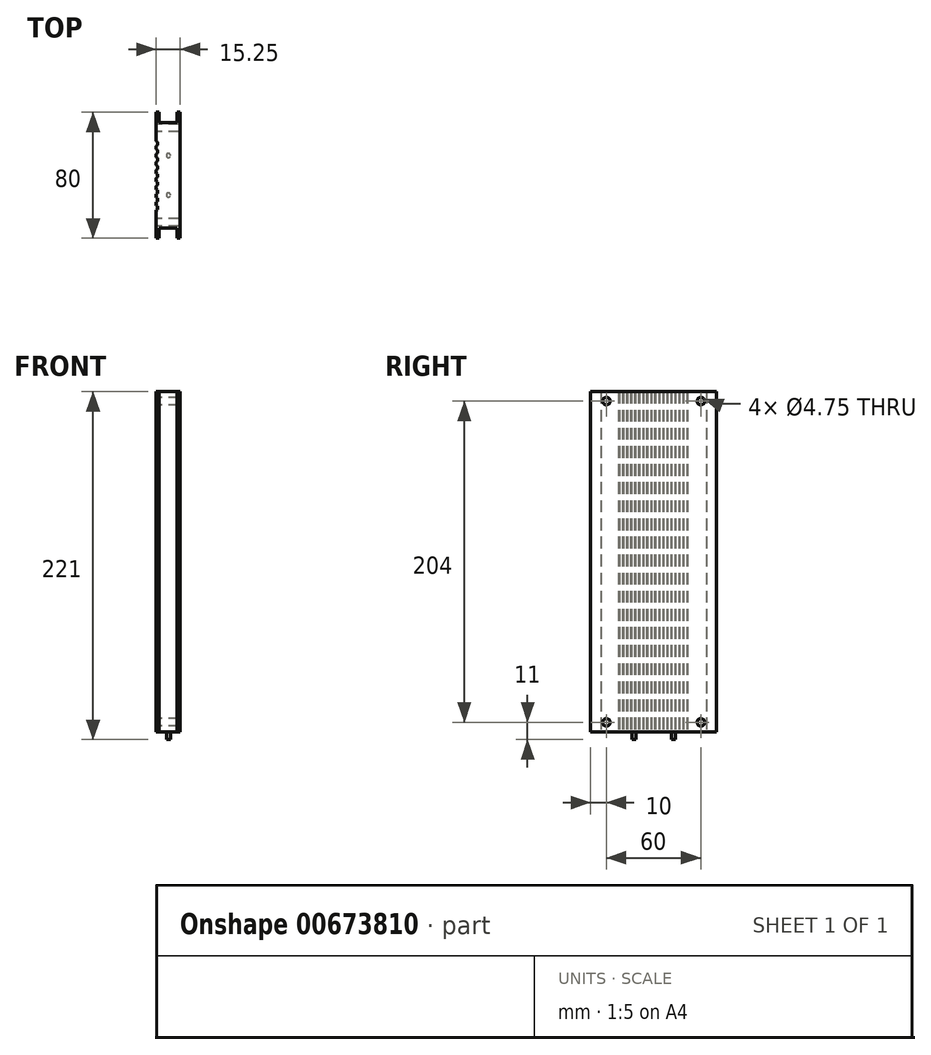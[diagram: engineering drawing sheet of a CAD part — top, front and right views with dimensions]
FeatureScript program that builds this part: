
annotation { "Feature Type Name" : "Feature", "Feature Type Description" : "" }
export const myFeature = defineFeature(function(context is Context, id is Id, definition is map)
    precondition{}
    {
        {
            var Q0;
            Q0=qCreatedBy(makeId("Top.planeOp"),FACE);
            var sketch = newSketch(context, id + "F0", { "sketchPlane" : qUnion([Q0])});
            skLineSegment(sketch, "E0", {"start": v(0, 0) * mm, "end": v(0, 80) * mm});
            skLineSegment(sketch, "E1", {"start": v(0, 80) * mm, "end": v(1.9, 80) * mm});
            skLineSegment(sketch, "E2", {"start": v(1.9, 80) * mm, "end": v(1.9, 73.55) * mm});
            skLineSegment(sketch, "E3", {"start": v(1.9, 73.55) * mm, "end": v(13.35, 73.55) * mm});
            skLineSegment(sketch, "E4", {"start": v(13.35, 73.55) * mm, "end": v(13.35, 80) * mm});
            skLineSegment(sketch, "E5", {"start": v(13.35, 80) * mm, "end": v(15.25, 80) * mm});
            skLineSegment(sketch, "E6", {"start": v(15.25, 80) * mm, "end": v(15.25, 0) * mm});
            skLineSegment(sketch, "E7", {"start": v(15.25, 0) * mm, "end": v(13.35, 0) * mm});
            skLineSegment(sketch, "E8", {"start": v(13.35, 0) * mm, "end": v(13.35, 6.45) * mm});
            skLineSegment(sketch, "E9", {"start": v(13.35, 6.45) * mm, "end": v(1.9, 6.45) * mm});
            skLineSegment(sketch, "E10", {"start": v(1.9, 6.45) * mm, "end": v(1.9, 0) * mm});
            skLineSegment(sketch, "E11", {"start": v(1.9, 0) * mm, "end": v(0, 0) * mm});
            skPoint(sketch, "E12", {"position": v(0, 61.6) * mm});
            skLineSegment(sketch, "E13", {"start": v(0, 61.6) * mm, "end": v(1, 61.1) * mm});
            skLineSegment(sketch, "E14", {"start": v(1, 61.1) * mm, "end": v(1, 59.1) * mm});
            skLineSegment(sketch, "E15", {"start": v(1, 59.1) * mm, "end": v(0, 58.6) * mm});
            skLineSegment(sketch, "E16", {"start": v(0, 58.6) * mm, "end": v(0, 61.6) * mm});
            skLineSegment(sketch, "E17.0.1.0", {"start": v(0, 56.5) * mm, "end": v(1, 56) * mm});
            skPoint(sketch, "E17.0.1.1", {"position": v(0, 56.5) * mm});
            skLineSegment(sketch, "E17.0.1.2", {"start": v(0, 53.5) * mm, "end": v(0, 56.5) * mm});
            skLineSegment(sketch, "E17.0.1.3", {"start": v(1, 54) * mm, "end": v(0, 53.5) * mm});
            skLineSegment(sketch, "E17.0.1.4", {"start": v(1, 56) * mm, "end": v(1, 54) * mm});
            skLineSegment(sketch, "E17.0.2.0", {"start": v(0, 51.4) * mm, "end": v(1, 50.9) * mm});
            skPoint(sketch, "E17.0.2.1", {"position": v(0, 51.4) * mm});
            skLineSegment(sketch, "E17.0.2.2", {"start": v(0, 48.4) * mm, "end": v(0, 51.4) * mm});
            skLineSegment(sketch, "E17.0.2.3", {"start": v(1, 48.9) * mm, "end": v(0, 48.4) * mm});
            skLineSegment(sketch, "E17.0.2.4", {"start": v(1, 50.9) * mm, "end": v(1, 48.9) * mm});
            skLineSegment(sketch, "E17.0.3.0", {"start": v(0, 46.3) * mm, "end": v(1, 45.8) * mm});
            skPoint(sketch, "E17.0.3.1", {"position": v(0, 46.3) * mm});
            skLineSegment(sketch, "E17.0.3.2", {"start": v(0, 43.3) * mm, "end": v(0, 46.3) * mm});
            skLineSegment(sketch, "E17.0.3.3", {"start": v(1, 43.8) * mm, "end": v(0, 43.3) * mm});
            skLineSegment(sketch, "E17.0.3.4", {"start": v(1, 45.8) * mm, "end": v(1, 43.8) * mm});
            skLineSegment(sketch, "E17.0.4.0", {"start": v(0, 41.2) * mm, "end": v(1, 40.7) * mm});
            skPoint(sketch, "E17.0.4.1", {"position": v(0, 41.2) * mm});
            skLineSegment(sketch, "E17.0.4.2", {"start": v(0, 38.2) * mm, "end": v(0, 41.2) * mm});
            skLineSegment(sketch, "E17.0.4.3", {"start": v(1, 38.7) * mm, "end": v(0, 38.2) * mm});
            skLineSegment(sketch, "E17.0.4.4", {"start": v(1, 40.7) * mm, "end": v(1, 38.7) * mm});
            skLineSegment(sketch, "E17.0.5.0", {"start": v(0, 36.1) * mm, "end": v(1, 35.6) * mm});
            skPoint(sketch, "E17.0.5.1", {"position": v(0, 36.1) * mm});
            skLineSegment(sketch, "E17.0.5.2", {"start": v(0, 33.1) * mm, "end": v(0, 36.1) * mm});
            skLineSegment(sketch, "E17.0.5.3", {"start": v(1, 33.6) * mm, "end": v(0, 33.1) * mm});
            skLineSegment(sketch, "E17.0.5.4", {"start": v(1, 35.6) * mm, "end": v(1, 33.6) * mm});
            skLineSegment(sketch, "E17.0.6.0", {"start": v(0, 31) * mm, "end": v(1, 30.5) * mm});
            skPoint(sketch, "E17.0.6.1", {"position": v(0, 31) * mm});
            skLineSegment(sketch, "E17.0.6.2", {"start": v(0, 28) * mm, "end": v(0, 31) * mm});
            skLineSegment(sketch, "E17.0.6.3", {"start": v(1, 28.5) * mm, "end": v(0, 28) * mm});
            skLineSegment(sketch, "E17.0.6.4", {"start": v(1, 30.5) * mm, "end": v(1, 28.5) * mm});
            skLineSegment(sketch, "E17.0.7.0", {"start": v(0, 25.9) * mm, "end": v(1, 25.4) * mm});
            skPoint(sketch, "E17.0.7.1", {"position": v(0, 25.9) * mm});
            skLineSegment(sketch, "E17.0.7.2", {"start": v(0, 22.9) * mm, "end": v(0, 25.9) * mm});
            skLineSegment(sketch, "E17.0.7.3", {"start": v(1, 23.4) * mm, "end": v(0, 22.9) * mm});
            skLineSegment(sketch, "E17.0.7.4", {"start": v(1, 25.4) * mm, "end": v(1, 23.4) * mm});
            skLineSegment(sketch, "E17.0.8.0", {"start": v(0, 20.8) * mm, "end": v(1, 20.3) * mm});
            skPoint(sketch, "E17.0.8.1", {"position": v(0, 20.8) * mm});
            skLineSegment(sketch, "E17.0.8.2", {"start": v(0, 17.8) * mm, "end": v(0, 20.8) * mm});
            skLineSegment(sketch, "E17.0.8.3", {"start": v(1, 18.3) * mm, "end": v(0, 17.8) * mm});
            skLineSegment(sketch, "E17.0.8.4", {"start": v(1, 20.3) * mm, "end": v(1, 18.3) * mm});
            skLineSegment(sketch, "E17.direction1", {"start": v(0, 58.6) * mm, "end": v(25, 58.6) * mm, "construction": true});
            skLineSegment(sketch, "E17.direction2", {"start": v(0, 58.6) * mm, "end": v(0, 53.5) * mm, "construction": true});
            skSolve(sketch);
        }
        {
            var Q0;
            {var subQ3=sQuery(id+"F0.wireOp",EDGE,"E1");Q0=makeQuery(id+"F0.imprint","IMPRINT",FACE,{"disambiguationData":[TD([[makeQuery(id+"F0.imprint","IMPRINT",EDGE,{"derivedFrom":subQ3}),-1.0]])]});}
            extrude(context, id + "F1", {"entities" : qUnion([Q0]), "depth" : 216 * mm, "offsetDistance" : 25 * mm});
        }
        {
            var Q0;
            {var subQ0=sQuery(id+"F0.wireOp",EDGE,"E0");Q0=makeQuery(id+"F1.opExtrude","SWEPT_FACE",FACE,{"disambiguationData":[OSD([subQ0]),TDD([makeQuery(id+"F0.imprint","IMPRINT",EDGE,{"disambiguationData":[TD([[makeQuery(id+"F0.imprint","INTERSECT",VERTEX,{"derivedFrom":[subQ0,sQuery(id+"F0.wireOp",EDGE,"E1")]}),1.0]])],"derivedFrom":subQ0})])]});}
            var sketch = newSketch(context, id + "F2", { "sketchPlane" : qUnion([Q0])});
            skCircle(sketch, "E18", {"center": v(-70, 6) * mm, "radius": 2.38 * mm});
            skCircle(sketch, "E19", {"center": v(-10, 6) * mm, "radius": 2.38 * mm});
            skCircle(sketch, "E20", {"center": v(-70, 210) * mm, "radius": 2.38 * mm});
            skCircle(sketch, "E21", {"center": v(-10, 210) * mm, "radius": 2.38 * mm});
            skSolve(sketch);
        }
        {
            var Q0;
            Q0 = qSketchRegion(id + "F2", true);
            extrude(context, id + "F3", {"entities" : qUnion([Q0]), "operationType" : NewBodyOperationType.REMOVE, "endBound" : BoundingType.THROUGH_ALL, "oppositeDirection" : true, "depth" : 25 * mm, "offsetDistance" : 25 * mm});
        }
        {
            var Q0;
            Q0=makeQuery(id+"F1.opExtrude","CAP_FACE",FACE,{"disambiguationData":[OSD([sQuery(id+"F0.wireOp",EDGE,"E0"),sQuery(id+"F0.wireOp",EDGE,"E1"),sQuery(id+"F0.wireOp",EDGE,"E2"),sQuery(id+"F0.wireOp",EDGE,"E3"),sQuery(id+"F0.wireOp",EDGE,"E4"),sQuery(id+"F0.wireOp",EDGE,"E5"),sQuery(id+"F0.wireOp",EDGE,"E6"),sQuery(id+"F0.wireOp",EDGE,"E7"),sQuery(id+"F0.wireOp",EDGE,"E8"),sQuery(id+"F0.wireOp",EDGE,"E9"),sQuery(id+"F0.wireOp",EDGE,"E10"),sQuery(id+"F0.wireOp",EDGE,"E11"),sQuery(id+"F0.wireOp",EDGE,"E13"),sQuery(id+"F0.wireOp",EDGE,"E14"),sQuery(id+"F0.wireOp",EDGE,"E15"),sQuery(id+"F0.wireOp",EDGE,"E17.0.1.0"),sQuery(id+"F0.wireOp",EDGE,"E17.0.1.3"),sQuery(id+"F0.wireOp",EDGE,"E17.0.1.4"),sQuery(id+"F0.wireOp",EDGE,"E17.0.2.0"),sQuery(id+"F0.wireOp",EDGE,"E17.0.2.3"),sQuery(id+"F0.wireOp",EDGE,"E17.0.2.4"),sQuery(id+"F0.wireOp",EDGE,"E17.0.3.0"),sQuery(id+"F0.wireOp",EDGE,"E17.0.3.3"),sQuery(id+"F0.wireOp",EDGE,"E17.0.3.4"),sQuery(id+"F0.wireOp",EDGE,"E17.0.4.0"),sQuery(id+"F0.wireOp",EDGE,"E17.0.4.3"),sQuery(id+"F0.wireOp",EDGE,"E17.0.4.4"),sQuery(id+"F0.wireOp",EDGE,"E17.0.5.0"),sQuery(id+"F0.wireOp",EDGE,"E17.0.5.3"),sQuery(id+"F0.wireOp",EDGE,"E17.0.5.4"),sQuery(id+"F0.wireOp",EDGE,"E17.0.6.0"),sQuery(id+"F0.wireOp",EDGE,"E17.0.6.3"),sQuery(id+"F0.wireOp",EDGE,"E17.0.6.4"),sQuery(id+"F0.wireOp",EDGE,"E17.0.7.0"),sQuery(id+"F0.wireOp",EDGE,"E17.0.7.3"),sQuery(id+"F0.wireOp",EDGE,"E17.0.7.4"),sQuery(id+"F0.wireOp",EDGE,"E17.0.8.0"),sQuery(id+"F0.wireOp",EDGE,"E17.0.8.3"),sQuery(id+"F0.wireOp",EDGE,"E17.0.8.4")])],"isStart":true});
            var sketch = newSketch(context, id + "F4", { "sketchPlane" : qUnion([Q0])});
            skCircle(sketch, "E22", {"center": v(7.79, -52.55) * mm, "radius": 1.3 * mm});
            skCircle(sketch, "E23", {"center": v(7.79, -27.45) * mm, "radius": 1.3 * mm});
            skSolve(sketch);
        }
        {
            var Q0;
            Q0=makeQuery(id+"F4.imprint","IMPRINT",FACE,{"disambiguationData":[TD([[makeQuery(id+"F4.imprint","IMPRINT",EDGE,{"derivedFrom":sQuery(id+"F4.wireOp",EDGE,"E23")}),1.0]])]});
            extrude(context, id + "F5", {"entities" : qUnion([Q0]), "depth" : 5 * mm, "offsetDistance" : 25 * mm});
        }
        {
            var Q0;
            Q0=makeQuery(id+"F4.imprint","IMPRINT",FACE,{"disambiguationData":[TD([[makeQuery(id+"F4.imprint","IMPRINT",EDGE,{"derivedFrom":sQuery(id+"F4.wireOp",EDGE,"E22")}),1.0]])]});
            extrude(context, id + "F6", {"entities" : qUnion([Q0]), "depth" : 5 * mm, "offsetDistance" : 25 * mm});
        }
    });
